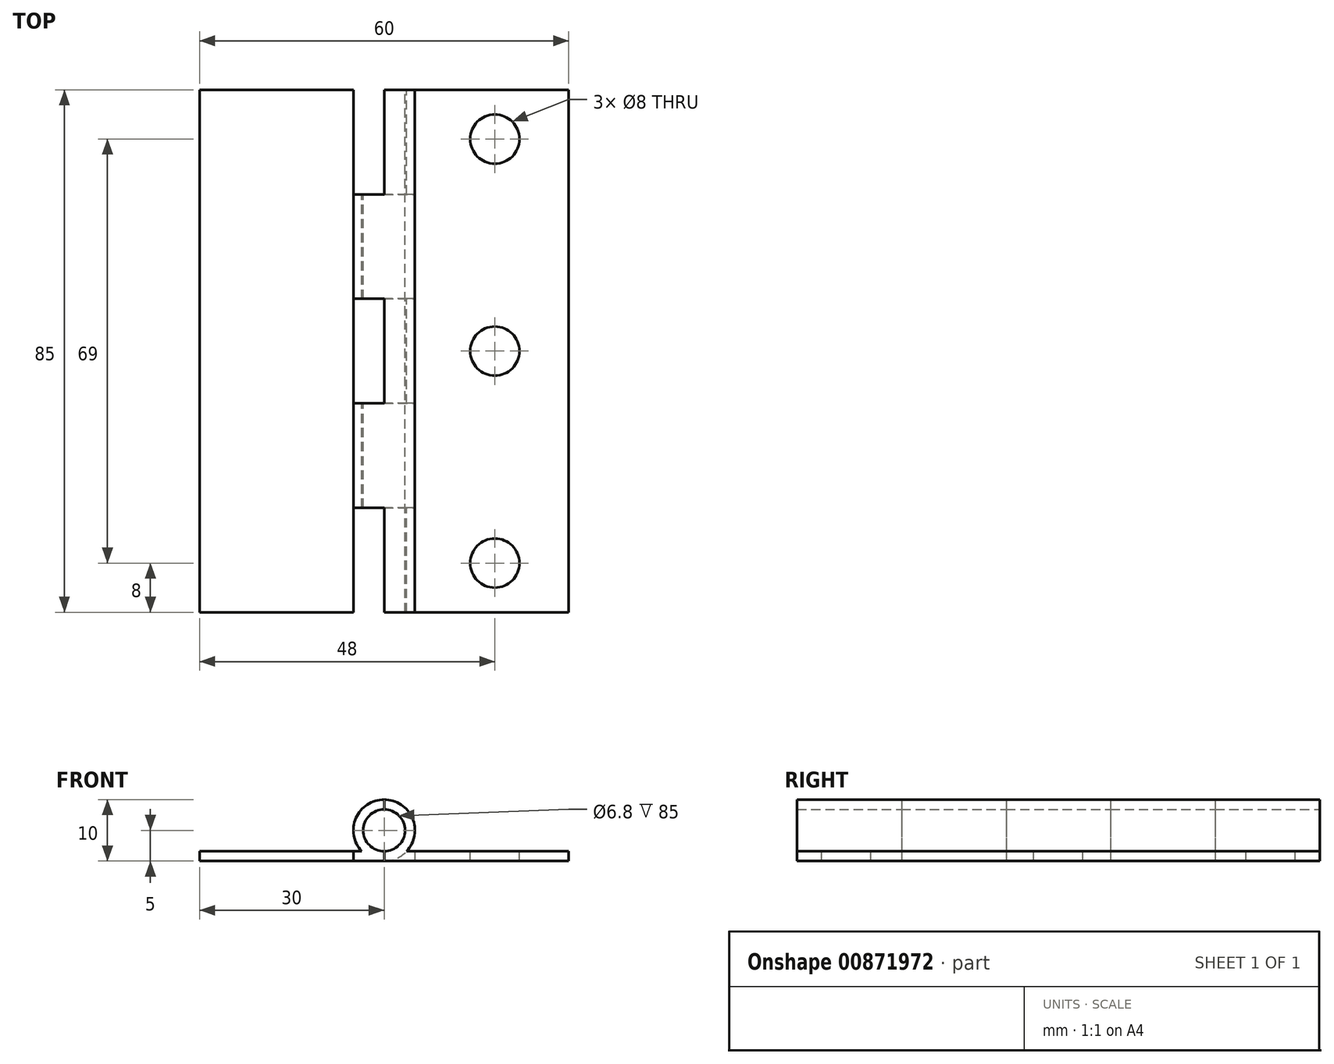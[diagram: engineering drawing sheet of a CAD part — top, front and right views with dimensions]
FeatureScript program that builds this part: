
annotation { "Feature Type Name" : "Feature", "Feature Type Description" : "" }
export const myFeature = defineFeature(function(context is Context, id is Id, definition is map)
    precondition{}
    {
        {
            var Q0;
            Q0=qCreatedBy(makeId("Front.planeOp"),FACE);
            var sketch = newSketch(context, id + "F0", { "sketchPlane" : qUnion([Q0])});
            skCircle(sketch, "E0", {"center": v(0, 0) * mm, "radius": 5 * mm});
            skCircle(sketch, "E1", {"center": v(0, 0) * mm, "radius": 3.4 * mm});
            skSolve(sketch);
        }
        {
            var Q0;
            Q0 = qSketchRegion(id + "F0", true);
            extrude(context, id + "F1", {"entities" : qUnion([Q0]), "endBound" : BoundingType.SYMMETRIC, "depth" : 85 * mm, "offsetDistance" : 25 * mm});
        }
        {
            var Q0;
            Q0=qCreatedBy(makeId("Front.planeOp"),FACE);
            var sketch = newSketch(context, id + "F2", { "sketchPlane" : qUnion([Q0])});
            skLineSegment(sketch, "E2.bottom", {"start": v(0, -5) * mm, "end": v(30, -5) * mm});
            skLineSegment(sketch, "E2.top", {"start": v(0, -3.4) * mm, "end": v(30, -3.4) * mm});
            skLineSegment(sketch, "E2.left", {"start": v(0, -5) * mm, "end": v(0, -3.4) * mm});
            skLineSegment(sketch, "E2.right", {"start": v(30, -5) * mm, "end": v(30, -3.4) * mm});
            skSolve(sketch);
        }
        {
            var Q0;
            Q0 = qSketchRegion(id + "F2", true);
            extrude(context, id + "F3", {"entities" : qUnion([Q0]), "operationType" : NewBodyOperationType.ADD, "endBound" : BoundingType.SYMMETRIC, "depth" : 85 * mm, "offsetDistance" : 25 * mm});
        }
        {
            var Q0;
            Q0=makeQuery(id+"F3.opExtrude","SWEPT_FACE",FACE,{"disambiguationData":[OSD([sQuery(id+"F2.wireOp",EDGE,"E2.bottom")])]});
            var sketch = newSketch(context, id + "F4", { "sketchPlane" : qUnion([Q0])});
            skLineSegment(sketch, "E3.bottom", {"start": v(-5, 25.5) * mm, "end": v(5, 25.5) * mm});
            skLineSegment(sketch, "E3.top", {"start": v(-5, 8.5) * mm, "end": v(5, 8.5) * mm});
            skLineSegment(sketch, "E3.left", {"start": v(-5, 25.5) * mm, "end": v(-5, 8.5) * mm});
            skLineSegment(sketch, "E3.right", {"start": v(5, 25.5) * mm, "end": v(5, 8.5) * mm});
            skLineSegment(sketch, "E4.bottom", {"start": v(-5, -8.5) * mm, "end": v(5, -8.5) * mm});
            skLineSegment(sketch, "E4.top", {"start": v(-5, -25.5) * mm, "end": v(5, -25.5) * mm});
            skLineSegment(sketch, "E4.left", {"start": v(-5, -8.5) * mm, "end": v(-5, -25.5) * mm});
            skLineSegment(sketch, "E4.right", {"start": v(5, -8.5) * mm, "end": v(5, -25.5) * mm});
            skLineSegment(sketch, "E5", {"start": v(0, 42.5) * mm, "end": v(0, 25.5) * mm, "construction": true});
            skLineSegment(sketch, "E6", {"start": v(0, 8.5) * mm, "end": v(0, -8.5) * mm, "construction": true});
            skLineSegment(sketch, "E7", {"start": v(0, -25.5) * mm, "end": v(0, -42.5) * mm, "construction": true});
            skLineSegment(sketch, "E8.0", {"start": v(-5, 42.5) * mm, "end": v(5, 42.5) * mm, "construction": true});
            skSolve(sketch);
        }
        {
            var Q0;
            Q0 = qSketchRegion(id + "F4", true);
            extrude(context, id + "F5", {"entities" : qUnion([Q0]), "operationType" : NewBodyOperationType.REMOVE, "endBound" : BoundingType.THROUGH_ALL, "oppositeDirection" : true, "depth" : 25 * mm, "offsetDistance" : 25 * mm});
        }
        {
            var Q0;
            Q0=qCreatedBy(makeId("Front.planeOp"),FACE);
            var sketch = newSketch(context, id + "F6", { "sketchPlane" : qUnion([Q0])});
            skCircle(sketch, "E9.1", {"center": v(0, 0) * mm, "radius": 3.4 * mm});
            skCircle(sketch, "E10", {"center": v(0, 0) * mm, "radius": 5 * mm});
            skSolve(sketch);
        }
        {
            var Q0;
            Q0 = qSketchRegion(id + "F6", true);
            var Q1;
            Q1=makeQuery(id+"F3.boolean.opBoolean","MERGE",FACE,{"derivedFrom":[makeQuery(id+"F1.opExtrude","CAP_FACE",FACE,{"disambiguationData":[OSD([sQuery(id+"F0.wireOp",EDGE,"E0"),sQuery(id+"F0.wireOp",EDGE,"E1")])],"isStart":false}),makeQuery(id+"F3.opExtrude","CAP_FACE",FACE,{"disambiguationData":[OSD([sQuery(id+"F2.wireOp",EDGE,"E2.bottom"),sQuery(id+"F2.wireOp",EDGE,"E2.top"),sQuery(id+"F2.wireOp",EDGE,"E2.left"),sQuery(id+"F2.wireOp",EDGE,"E2.right")])],"isStart":false})]});
            var Q2;
            Q2=makeQuery(id+"F3.boolean.opBoolean","MERGE",FACE,{"derivedFrom":[makeQuery(id+"F1.opExtrude","CAP_FACE",FACE,{"disambiguationData":[OSD([sQuery(id+"F0.wireOp",EDGE,"E0"),sQuery(id+"F0.wireOp",EDGE,"E1")])],"isStart":true}),makeQuery(id+"F3.opExtrude","CAP_FACE",FACE,{"disambiguationData":[OSD([sQuery(id+"F2.wireOp",EDGE,"E2.bottom"),sQuery(id+"F2.wireOp",EDGE,"E2.top"),sQuery(id+"F2.wireOp",EDGE,"E2.left"),sQuery(id+"F2.wireOp",EDGE,"E2.right")])],"isStart":true})]});
            extrude(context, id + "F7", {"entities" : qUnion([Q0]), "endBound" : BoundingType.UP_TO_SURFACE, "depth" : 25 * mm, "endBoundEntityFace" : qUnion([Q1]), "offsetDistance" : 25 * mm, "hasSecondDirection" : true, "secondDirectionBound" : SecondDirectionBoundingType.UP_TO_SURFACE, "secondDirectionOppositeDirection" : true, "secondDirectionDepth" : 25 * mm, "secondDirectionBoundEntityFace" : qUnion([Q2])});
        }
        {
            var Q0;
            Q0=makeQuery(id+"F1.opExtrude","SWEPT_BODY",BODY,{"disambiguationData":[OSD([sQuery(id+"F0.wireOp",EDGE,"E0"),sQuery(id+"F0.wireOp",EDGE,"E1")])]});
            var Q1;
            Q1=makeQuery(id+"F7.opExtrude","SWEPT_BODY",BODY,{"disambiguationData":[OSD([sQuery(id+"F6.wireOp",EDGE,"E9.1"),sQuery(id+"F6.wireOp",EDGE,"E10")])]});
            booleanBodies(context, id + "F8", {"operationType" : BooleanOperationType.SUBTRACTION, "tools" : qUnion([Q0]), "targets" : qUnion([Q1]), "keepTools" : true});
        }
        {
            var Q0;
            Q0=qCreatedBy(makeId("Front.planeOp"),FACE);
            var sketch = newSketch(context, id + "F9", { "sketchPlane" : qUnion([Q0])});
            skLineSegment(sketch, "E11.bottom", {"start": v(0, -3.4) * mm, "end": v(-30, -3.4) * mm});
            skLineSegment(sketch, "E11.top", {"start": v(0, -5) * mm, "end": v(-30, -5) * mm});
            skLineSegment(sketch, "E11.left", {"start": v(0, -3.4) * mm, "end": v(0, -5) * mm});
            skLineSegment(sketch, "E11.right", {"start": v(-30, -3.4) * mm, "end": v(-30, -5) * mm});
            skSolve(sketch);
        }
        {
            var Q0;
            Q0 = qSketchRegion(id + "F9", true);
            var Q1;
            Q1=makeQuery(id+"F3.boolean.opBoolean","MERGE",FACE,{"derivedFrom":[makeQuery(id+"F1.opExtrude","CAP_FACE",FACE,{"disambiguationData":[OSD([sQuery(id+"F0.wireOp",EDGE,"E0"),sQuery(id+"F0.wireOp",EDGE,"E1")])],"isStart":false}),makeQuery(id+"F3.opExtrude","CAP_FACE",FACE,{"disambiguationData":[OSD([sQuery(id+"F2.wireOp",EDGE,"E2.bottom"),sQuery(id+"F2.wireOp",EDGE,"E2.top"),sQuery(id+"F2.wireOp",EDGE,"E2.left"),sQuery(id+"F2.wireOp",EDGE,"E2.right")])],"isStart":false})]});
            var Q2;
            Q2=makeQuery(id+"F3.boolean.opBoolean","MERGE",FACE,{"derivedFrom":[makeQuery(id+"F1.opExtrude","CAP_FACE",FACE,{"disambiguationData":[OSD([sQuery(id+"F0.wireOp",EDGE,"E0"),sQuery(id+"F0.wireOp",EDGE,"E1")])],"isStart":true}),makeQuery(id+"F3.opExtrude","CAP_FACE",FACE,{"disambiguationData":[OSD([sQuery(id+"F2.wireOp",EDGE,"E2.bottom"),sQuery(id+"F2.wireOp",EDGE,"E2.top"),sQuery(id+"F2.wireOp",EDGE,"E2.left"),sQuery(id+"F2.wireOp",EDGE,"E2.right")])],"isStart":true})]});
            extrude(context, id + "F10", {"entities" : qUnion([Q0]), "operationType" : NewBodyOperationType.ADD, "endBound" : BoundingType.UP_TO_SURFACE, "depth" : 25 * mm, "endBoundEntityFace" : qUnion([Q1]), "offsetDistance" : 25 * mm, "hasSecondDirection" : true, "secondDirectionBound" : SecondDirectionBoundingType.UP_TO_SURFACE, "secondDirectionOppositeDirection" : true, "secondDirectionDepth" : 25 * mm, "secondDirectionBoundEntityFace" : qUnion([Q2])});
        }
        {
            var Q0;
            Q0=makeQuery(id+"F10.opExtrude","SWEPT_FACE",FACE,{"disambiguationData":[OSD([sQuery(id+"F9.wireOp",EDGE,"E11.top")])]});
            var sketch = newSketch(context, id + "F11", { "sketchPlane" : qUnion([Q0])});
            skLineSegment(sketch, "E12.bottom", {"start": v(0, 42.5) * mm, "end": v(-5, 42.5) * mm});
            skLineSegment(sketch, "E12.top", {"start": v(0, 25.5) * mm, "end": v(-5, 25.5) * mm});
            skLineSegment(sketch, "E12.left", {"start": v(0, 42.5) * mm, "end": v(0, 25.5) * mm});
            skLineSegment(sketch, "E12.right", {"start": v(-5, 42.5) * mm, "end": v(-5, 25.5) * mm});
            skLineSegment(sketch, "E13.bottom", {"start": v(0, 8.5) * mm, "end": v(-5, 8.5) * mm});
            skLineSegment(sketch, "E13.top", {"start": v(0, -8.5) * mm, "end": v(-5, -8.5) * mm});
            skLineSegment(sketch, "E13.left", {"start": v(0, 8.5) * mm, "end": v(0, -8.5) * mm});
            skLineSegment(sketch, "E13.right", {"start": v(-5, 8.5) * mm, "end": v(-5, -8.5) * mm});
            skLineSegment(sketch, "E14.bottom", {"start": v(0, -42.5) * mm, "end": v(-5, -42.5) * mm});
            skLineSegment(sketch, "E14.top", {"start": v(0, -25.5) * mm, "end": v(-5, -25.5) * mm});
            skLineSegment(sketch, "E14.left", {"start": v(0, -42.5) * mm, "end": v(0, -25.5) * mm});
            skLineSegment(sketch, "E14.right", {"start": v(-5, -42.5) * mm, "end": v(-5, -25.5) * mm});
            skSolve(sketch);
        }
        {
            var Q0;
            Q0 = qSketchRegion(id + "F11", true);
            extrude(context, id + "F12", {"entities" : qUnion([Q0]), "operationType" : NewBodyOperationType.REMOVE, "endBound" : BoundingType.THROUGH_ALL, "oppositeDirection" : true, "depth" : 25 * mm, "offsetDistance" : 25 * mm});
        }
        {
            var Q0;
            Q0=makeQuery(id+"F3.opExtrude","SWEPT_FACE",FACE,{"disambiguationData":[OSD([sQuery(id+"F2.wireOp",EDGE,"E2.top")])]});
            var sketch = newSketch(context, id + "F13", { "sketchPlane" : qUnion([Q0])});
            skCircle(sketch, "E15", {"center": v(18, 34.5) * mm, "radius": 4 * mm});
            skCircle(sketch, "E16", {"center": v(18, 0) * mm, "radius": 4 * mm});
            skCircle(sketch, "E17", {"center": v(18, -34.5) * mm, "radius": 4 * mm});
            skSolve(sketch);
        }
        {
            var Q0;
            Q0 = qSketchRegion(id + "F13", true);
            extrude(context, id + "F14", {"entities" : qUnion([Q0]), "operationType" : NewBodyOperationType.REMOVE, "endBound" : BoundingType.THROUGH_ALL, "oppositeDirection" : true, "depth" : 25 * mm, "offsetDistance" : 25 * mm});
        }
    });
